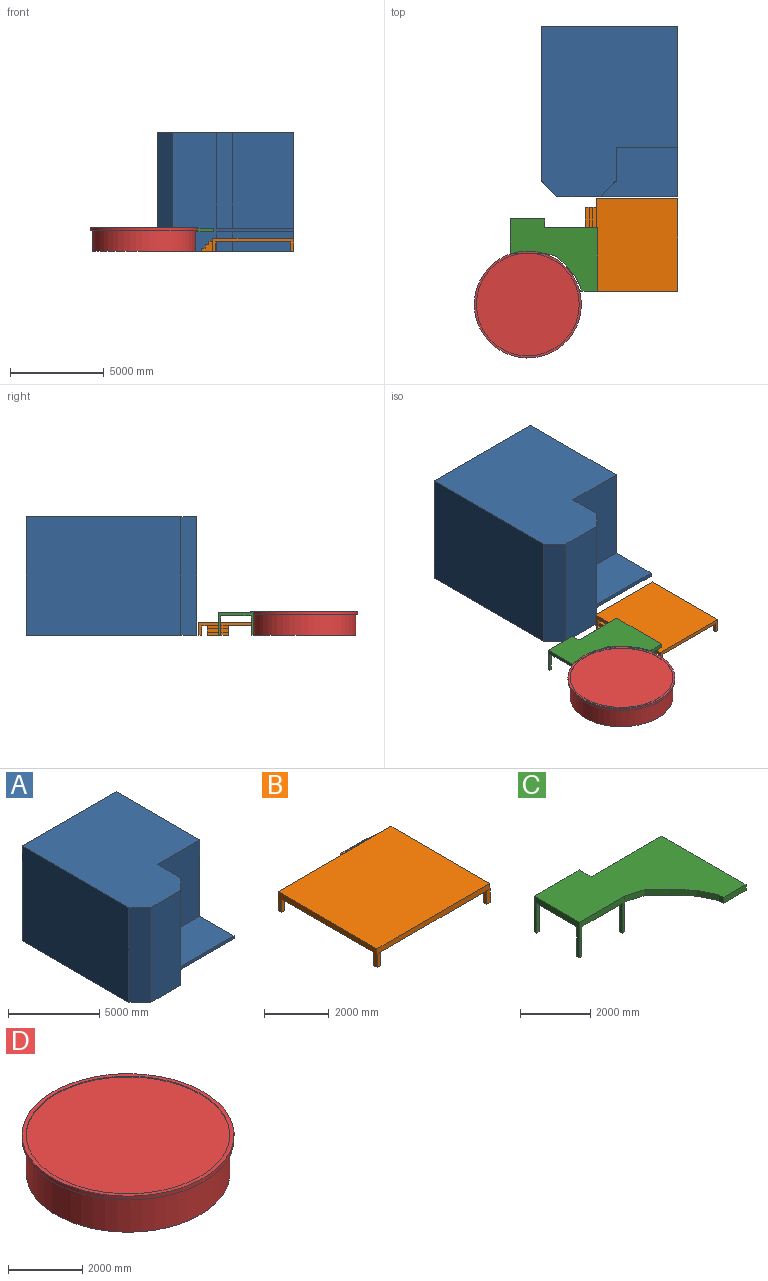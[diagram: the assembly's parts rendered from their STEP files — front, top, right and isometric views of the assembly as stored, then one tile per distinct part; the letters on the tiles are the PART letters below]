
ASSEMBLY  parts=4 mates=3
PART A: 15 faces, bbox 7276.3x9111.7x6350 mm
  f0: plane 3276.6x1041.4mm, normal (0,-1,0), area 3412251.2mm2, adj f7,f9,f12,f13
  f1: plane 5105.4x844.14mm, normal (0.71,-0.71,0), area 6094826.5mm2, adj f2,f5,f11,f14
  f2: plane 5105.4x1784.35mm, normal (1,0,0), area 9109820.5mm2, adj f1,f8,f11,f14
  f3: plane 8267.56x6350mm, normal (-1,0,0), area 52498984.5mm2, adj f4,f10,f11,f12
  f4: plane 6350x844.14mm, normal (-0.71,-0.71,0), area 7580630mm2, adj f3,f5,f11,f12
  f5: plane 6432.14x6350mm, normal (0,-1,0), area 15514725.2mm2, adj f1,f4,f6,f9,f11,f12,f13,f14
  f6: plane 1041.4x844.14mm, normal (0.71,-0.71,0), area 1243223.3mm2, adj f5,f7,f12,f13
  f7: plane 1784.35x1041.4mm, normal (1,0,0), area 1858222.1mm2, adj f0,f6,f12,f13
  f8: plane 5105.4x3276.6mm, normal (0,-1,0), area 16728353.6mm2, adj f2,f9,f11,f14
  f9: plane 9111.7x6350mm, normal (1,0,0), area 41702472mm2, adj f0,f5,f8,f10,f11,f12,f13,f14
  f10: plane 7276.29x6350mm, normal (0,1,0), area 46204429.8mm2, adj f3,f9,f11,f12
  f11: plane 9111.7x7276.29mm, normal (0,0,1), area 56974256.8mm2, adj f1,f2,f3,f4,f5,f8,f9,f10
  f12: plane 9111.7x7276.29mm, normal (0,0,-1), area 56974256.8mm2, adj f0,f3,f4,f5,f6,f7,f9,f10
  f13: plane 4120.74x2628.49mm, normal (0,0,-1), area 8968813.3mm2, adj f0,f5,f6,f7,f9
  f14: plane 4120.74x2628.49mm, normal (0,0,1), area 8968813.3mm2, adj f1,f2,f5,f8,f9
PART B: 32 faces, bbox 4927.6x4927.6x711.2 mm
  f0: plane 4927.6x711.2mm, normal (0,1,0), area 1127739.7mm2, adj f1,f2,f4,f5,f14,f18,f19,f21
  f1: plane 4318x711.2mm, normal (1,0,0), area 1031740.7mm2, adj f0,f3,f4,f5,f6,f8,f9,f10
  f2: plane 508x152.4mm, normal (-1,0,0), area 77419.2mm2, adj f0,f3,f4,f5
  f3: plane 508x152.4mm, normal (0,-1,0), area 77419.2mm2, adj f1,f2,f4,f5
  f4: plane 152.4x152.4mm, normal (0,0,-1), area 23225.8mm2, adj f0,f1,f2,f3
  f5: plane 4927.6x4315.46mm, normal (0,0,-1), area 21172750.4mm2, adj f0,f1,f2,f3,f6,f7,f12,f13
  f6: plane 508x152.4mm, normal (0,1,0), area 77419.2mm2, adj f1,f5,f7,f10
  f7: plane 508x152.4mm, normal (-1,0,0), area 77419.2mm2, adj f5,f6,f8,f9,f10
  f8: plane 508x152.4mm, normal (0,-1,0), area 77419.2mm2, adj f1,f7,f9,f10
  f9: plane 152.4x2.54mm, normal (0,0,1), area 386.5mm2, adj f1,f7,f8,f20
  f10: plane 152.4x152.4mm, normal (0,0,-1), area 23225.8mm2, adj f1,f6,f7,f8
  f11: plane 508x152.4mm, normal (0,-1,0), area 77419.2mm2, adj f12,f14,f15,f16
  f12: plane 508x152.4mm, normal (1,0,0), area 77419.2mm2, adj f5,f11,f13,f15,f16
  f13: plane 508x152.4mm, normal (0,1,0), area 77419.2mm2, adj f5,f12,f14,f16
  f14: plane 4318x711.2mm, normal (-1,0,0), area 1031740.7mm2, adj f0,f5,f11,f13,f15,f16,f17,f19
  f15: plane 152.4x2.54mm, normal (0,0,1), area 386.5mm2, adj f11,f12,f14,f20
  f16: plane 152.4x152.4mm, normal (0,0,-1), area 23225.8mm2, adj f11,f12,f13,f14
  f17: plane 508x152.4mm, normal (0,-1,0), area 77419.2mm2, adj f5,f14,f18,f19
  f18: plane 508x152.4mm, normal (1,0,0), area 77419.2mm2, adj f0,f5,f17,f19
  f19: plane 152.4x152.4mm, normal (0,0,-1), area 23225.8mm2, adj f0,f14,f17,f18
  f20: plane 4927.6x203.2mm, normal (0,-1,0), area 1001288.3mm2, adj f1,f5,f9,f14,f15,f21
  f21: plane 4927.6x4315.46mm, normal (0,0,1), area 21264880.5mm2, adj f0,f1,f14,f20
  f22: plane 1117.6x508mm, normal (0,-1,0), area 567740.8mm2, adj f5,f23,f30,f31
  f23: plane 1117.6x609.6mm, normal (0,0,-1), area 681289mm2, adj f22,f24,f30,f31
  f24: plane 1117.6x177.8mm, normal (0,1,0), area 198709.3mm2, adj f23,f25,f30,f31
  f25: plane 1117.6x203.2mm, normal (0,0,1), area 227096.3mm2, adj f24,f26,f30,f31
  f26: plane 1117.6x177.8mm, normal (0,1,0), area 198709.3mm2, adj f25,f27,f30,f31
  f27: plane 1117.6x203.2mm, normal (0,0,1), area 227096.3mm2, adj f26,f28,f30,f31
  f28: plane 1117.6x177.8mm, normal (0,1,0), area 198709.3mm2, adj f27,f29,f30,f31
  f29: plane 1117.6x203.2mm, normal (0,0,1), area 227096.3mm2, adj f0,f28,f30,f31
  f30: plane 609.6x533.4mm, normal (-1,0,0), area 216773.8mm2, adj f0,f22,f23,f24,f25,f26,f27,f28
  f31: plane 609.6x533.4mm, normal (1,0,0), area 216773.8mm2, adj f0,f22,f23,f24,f25,f26,f27,f28
PART C: 27 faces, bbox 4672.8x3869.6x1244.6 mm
  f0: plane 1041.4x101.6mm, normal (1,0,0), area 105806.2mm2, adj f6,f7,f9,f10
  f1: plane 1244.6x476.37mm, normal (1,0,0), area 202604.9mm2, adj f2,f4,f5,f6,f18,f20
  f2: plane 1828.8x1244.6mm, normal (0,1,0), area 583224.6mm2, adj f1,f3,f5,f6,f11,f16,f17,f18
  f3: plane 1041.4x101.6mm, normal (-1,0,0), area 105806.2mm2, adj f2,f4,f5,f6
  f4: plane 1041.4x101.6mm, normal (0,-1,0), area 105806.2mm2, adj f1,f3,f5,f6
  f5: plane 101.6x101.6mm, normal (0,0,-1), area 10322.6mm2, adj f1,f2,f3,f4
  f6: plane 4672.84x3869.6mm, normal (0,0,-1), area 10200386.5mm2, adj f0,f1,f2,f3,f4,f7,f8,f9
  f7: plane 1041.4x101.6mm, normal (0,1,0), area 105806.2mm2, adj f0,f6,f8,f10
  f8: plane 1041.4x101.6mm, normal (-1,0,0), area 105806.2mm2, adj f6,f7,f9,f10
  f9: plane 1828.8x1244.6mm, normal (0,-1,0), area 583224.6mm2, adj f0,f6,f8,f10,f11,f12,f14,f18
  f10: plane 101.6x101.6mm, normal (0,0,-1), area 10322.6mm2, adj f0,f7,f8,f9
  f11: plane 1828.8x1244.6mm, normal (-1,0,0), area 583224.6mm2, adj f2,f6,f9,f13,f14,f15,f17,f18
  f12: plane 1041.4x101.6mm, normal (1,0,0), area 105806.2mm2, adj f6,f9,f13,f14
  f13: plane 1041.4x101.6mm, normal (0,1,0), area 105806.2mm2, adj f6,f11,f12,f14
  f14: plane 101.6x101.6mm, normal (0,0,-1), area 10322.6mm2, adj f9,f11,f12,f13
  f15: plane 1041.4x101.6mm, normal (0,-1,0), area 105806.2mm2, adj f6,f11,f16,f17
  f16: plane 1041.4x101.6mm, normal (1,0,0), area 105806.2mm2, adj f2,f6,f15,f17
  f17: plane 101.6x101.6mm, normal (0,0,-1), area 10322.6mm2, adj f2,f11,f15,f16
  f18: plane 4672.84x3869.6mm, normal (0,0,1), area 10241676.8mm2, adj f1,f2,f9,f11,f19,f20,f21,f22
  f19: plane 3393.23x203.2mm, normal (1,0,0), area 689504.3mm2, adj f6,f18,f20,f26
  f20: plane 2844.04x203.2mm, normal (0,1,0), area 577908.1mm2, adj f1,f6,f18,f19
  f21: plane 636.79x203.2mm, normal (-0.27,-0.96,0), area 134436.3mm2, adj f6,f9,f18,f22
  f22: plane 527.1x510.63mm, normal (-0.7,-0.72,0), area 149124.8mm2, adj f6,f18,f21,f23
  f23: plane 543.58x477.69mm, normal (-0.75,-0.66,0), area 147044.4mm2, adj f6,f18,f22,f24
  f24: plane 609.46x296.5mm, normal (-0.9,-0.44,0), area 137720.5mm2, adj f6,f18,f23,f25
  f25: plane 203.2x197.66mm, normal (-1,0,0), area 40165.3mm2, adj f6,f18,f24,f26
  f26: plane 905.96x203.2mm, normal (0,-1,0), area 184090.9mm2, adj f6,f18,f19,f25
PART D: 7 faces, bbox 5715x5715x1270 mm
  f0: cylinder r=2743.2mm len=5486.4mm, axis (0,0,-1), area 19700786.8mm2, adj f1,f4
  f1: plane 5486.4x5486.4mm, normal (0,0,-1), area 23640944.1mm2, adj f0
  f2: cylinder r=2743.2mm len=5486.4mm, axis (0,0,1), area 437795.3mm2, adj f5,f6
  f3: cylinder r=2857.5mm len=5715mm, axis (0,0,1), area 2280183.7mm2, adj f4,f5
  f4: plane 5715x5715mm, normal (0,0,-1), area 2011122mm2, adj f0,f3
  f5: plane 5715x5715mm, normal (0,0,1), area 2011122mm2, adj f2,f3
  f6: plane 5486.4x5486.4mm, normal (0,0,1), area 23640944.1mm2, adj f2
PLACE A at identity fixed
PLACE B rot(axis=(0,0,1),90deg) t=(2971.19,-2737.21,0)mm
PLACE C t=(186,-3803.74,0)mm
PLACE D t=(-709.75,-8377.64,0)mm
MATE planar B.f4 <-> A.f12  axis (0,0,-1) through (3047.39,-2813.41,0)mm
MATE planar D.f0 <-> A.f12  axis (0,0,-1) through (-709.75,-8377.64,0)mm
MATE planar C.f10 <-> D.f0  axis (0,0,-1) through (135.2,-5581.74,0)mm
